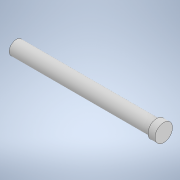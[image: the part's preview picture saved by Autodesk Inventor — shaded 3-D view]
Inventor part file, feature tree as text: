
AUTODESK INVENTOR PART (.ipt)
format: ipt  version: 2020 (Build 240168000, 168)  size: 102,400 bytes
history: native  units: mm
features: extrude x2, sketch x2
ambient origin geometry x8: Origin, YZ Plane, XZ Plane, XY Plane, X Axis, Y Axis, Z Axis, Center Point
bodies: Solid1 (feature_tree)
feature tree (4):
  extrude  "Extrusion1"  Depth=40.0mm TaperAngle=0.0deg
  extrude  "Extrusion2"  Depth=2.0mm TaperAngle=0.0deg
  sketch  "Sketch1"  dims[d0=4.0mm d1=40.0mm d2=0.0mm]
  sketch  "Sketch2"  dims[d3=5.0mm d4=2.0mm d5=0.0mm]
